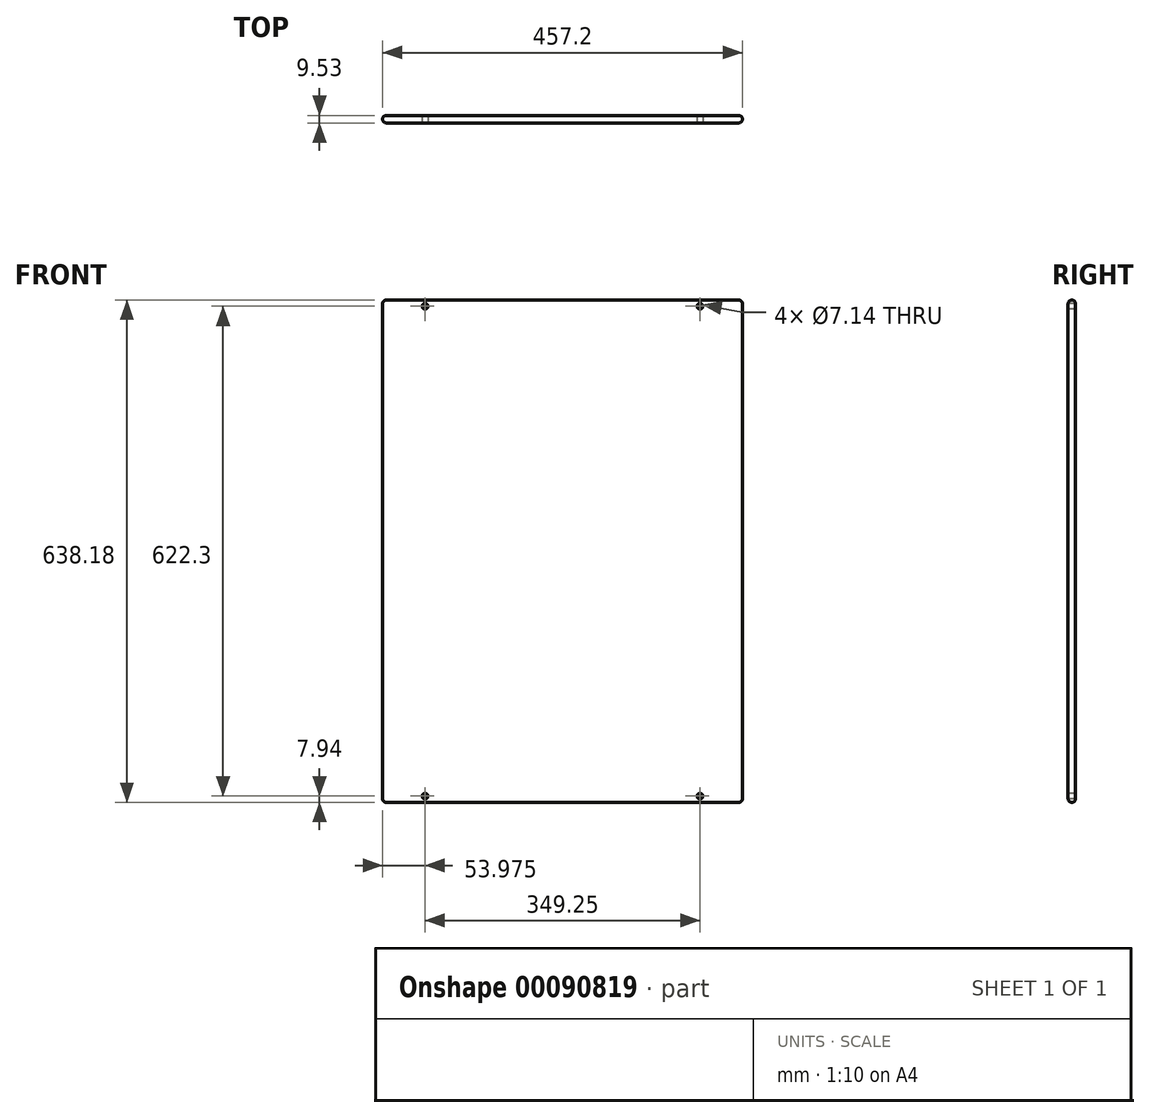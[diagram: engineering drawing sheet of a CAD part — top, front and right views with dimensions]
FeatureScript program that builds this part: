
annotation { "Feature Type Name" : "Feature", "Feature Type Description" : "" }
export const myFeature = defineFeature(function(context is Context, id is Id, definition is map)
    precondition{}
    {
        {
            var Q0;
            Q0=qCreatedBy(makeId("Front.planeOp"),FACE);
            var sketch = newSketch(context, id + "F0", { "sketchPlane" : qUnion([Q0])});
            skLineSegment(sketch, "E0.bottom", {"start": v(228.6, -319.09) * mm, "end": v(-228.6, -319.09) * mm});
            skLineSegment(sketch, "E0.top", {"start": v(228.6, 319.09) * mm, "end": v(-228.6, 319.09) * mm});
            skLineSegment(sketch, "E0.left", {"start": v(228.6, -319.09) * mm, "end": v(228.6, 319.09) * mm});
            skLineSegment(sketch, "E0.right", {"start": v(-228.6, -319.09) * mm, "end": v(-228.6, 319.09) * mm});
            skPoint(sketch, "E0.middle", {"position": v(0, 0) * mm});
            skSolve(sketch);
        }
        {
            var Q0;
            Q0=makeQuery(id+"F0.imprint","IMPRINT",FACE,{"disambiguationData":[TD([[makeQuery(id+"F0.imprint","IMPRINT",EDGE,{"derivedFrom":sQuery(id+"F0.wireOp",EDGE,"E0.bottom")}),-1.0]])]});
            extrude(context, id + "F1", {"entities" : qUnion([Q0]), "depth" : 9.52 * mm});
        }
        {
            var Q0;
            Q0=makeQuery(id+"F1.opExtrude","CAP_FACE",FACE,{"disambiguationData":[OSD([sQuery(id+"F0.wireOp",EDGE,"E0.bottom"),sQuery(id+"F0.wireOp",EDGE,"E0.top"),sQuery(id+"F0.wireOp",EDGE,"E0.left"),sQuery(id+"F0.wireOp",EDGE,"E0.right")])],"isStart":false});
            var sketch = newSketch(context, id + "F2", { "sketchPlane" : qUnion([Q0])});
            skLineSegment(sketch, "E1", {"start": v(0, 319.09) * mm, "end": v(0, -319.09) * mm, "construction": true});
            skLineSegment(sketch, "E2", {"start": v(-228.6, 0) * mm, "end": v(228.6, 0) * mm, "construction": true});
            skPoint(sketch, "E3", {"position": v(-174.62, 311.15) * mm});
            skPoint(sketch, "E4.MirrorP", {"position": v(174.63, 311.15) * mm});
            skPoint(sketch, "E5.MirrorP", {"position": v(174.63, -311.15) * mm});
            skPoint(sketch, "E6.MirrorP", {"position": v(-174.63, -311.15) * mm});
            skSolve(sketch);
        }
        {
            var Q0;
            Q0=sQuery(id+"F2.wireOp",VERTEX,"E3");
            var Q1;
            Q1=sQuery(id+"F2.wireOp",VERTEX,"E4.MirrorP");
            var Q2;
            Q2=sQuery(id+"F2.wireOp",VERTEX,"E6.MirrorP");
            var Q3;
            Q3=sQuery(id+"F2.wireOp",VERTEX,"E5.MirrorP");
            var Q4;
            Q4=makeQuery(id+"F1.opExtrude","SWEPT_BODY",BODY,{"disambiguationData":[OSD([sQuery(id+"F0.wireOp",EDGE,"E0.bottom"),sQuery(id+"F0.wireOp",EDGE,"E0.top"),sQuery(id+"F0.wireOp",EDGE,"E0.left"),sQuery(id+"F0.wireOp",EDGE,"E0.right")])]});
            hole(context, id + "F3", {"style" : HoleStyle.SIMPLE, "endStyle" : HoleEndStyle.THROUGH, "holeDiameter" : 7.14 * mm, "startFromSketch" : true, "locations" : qUnion([Q0, Q1, Q2, Q3]), "scope" : qUnion([Q4]), "isTappedThrough" : true});
        }
        {
            var Q0;
            Q0=makeQuery(id+"F1.opExtrude","CAP_EDGE",EDGE,{"disambiguationData":[OSD([sQuery(id+"F0.wireOp",EDGE,"E0.right")])],"isStart":false});
            var Q1;
            Q1=makeQuery(id+"F1.opExtrude","CAP_EDGE",EDGE,{"disambiguationData":[OSD([sQuery(id+"F0.wireOp",EDGE,"E0.bottom")])],"isStart":false});
            var Q2;
            Q2=makeQuery(id+"F1.opExtrude","CAP_EDGE",EDGE,{"disambiguationData":[OSD([sQuery(id+"F0.wireOp",EDGE,"E0.left")])],"isStart":false});
            var Q3;
            Q3=makeQuery(id+"F1.opExtrude","CAP_EDGE",EDGE,{"disambiguationData":[OSD([sQuery(id+"F0.wireOp",EDGE,"E0.top")])],"isStart":false});
            var Q4;
            Q4=makeQuery(id+"F1.opExtrude","CAP_EDGE",EDGE,{"disambiguationData":[OSD([sQuery(id+"F0.wireOp",EDGE,"E0.left")])],"isStart":true});
            var Q5;
            Q5=makeQuery(id+"F1.opExtrude","CAP_EDGE",EDGE,{"disambiguationData":[OSD([sQuery(id+"F0.wireOp",EDGE,"E0.top")])],"isStart":true});
            var Q6;
            Q6=makeQuery(id+"F1.opExtrude","CAP_EDGE",EDGE,{"disambiguationData":[OSD([sQuery(id+"F0.wireOp",EDGE,"E0.right")])],"isStart":true});
            var Q7;
            Q7=makeQuery(id+"F1.opExtrude","CAP_EDGE",EDGE,{"disambiguationData":[OSD([sQuery(id+"F0.wireOp",EDGE,"E0.bottom")])],"isStart":true});
            var Q8;
            Q8=makeQuery(id+"F1.opExtrude","SWEPT_EDGE",EDGE,{"disambiguationData":[OSD([sQuery(id+"F0.wireOp",EDGE,"E0.bottom"),sQuery(id+"F0.wireOp",EDGE,"E0.right")])]});
            var Q9;
            Q9=makeQuery(id+"F1.opExtrude","SWEPT_EDGE",EDGE,{"disambiguationData":[OSD([sQuery(id+"F0.wireOp",EDGE,"E0.bottom"),sQuery(id+"F0.wireOp",EDGE,"E0.left")])]});
            var Q10;
            Q10=makeQuery(id+"F1.opExtrude","SWEPT_EDGE",EDGE,{"disambiguationData":[OSD([sQuery(id+"F0.wireOp",EDGE,"E0.top"),sQuery(id+"F0.wireOp",EDGE,"E0.left")])]});
            var Q11;
            Q11=makeQuery(id+"F1.opExtrude","SWEPT_EDGE",EDGE,{"disambiguationData":[OSD([sQuery(id+"F0.wireOp",EDGE,"E0.top"),sQuery(id+"F0.wireOp",EDGE,"E0.right")])]});
            fillet(context, id + "F4", {"entities" : qUnion([Q0, Q1, Q2, Q3, Q4, Q5, Q6, Q7, Q8, Q9, Q10, Q11]), "radius" : 4.76 * mm, "tangentPropagation" : true, "allowEdgeOverflow" : false});
        }
    });
